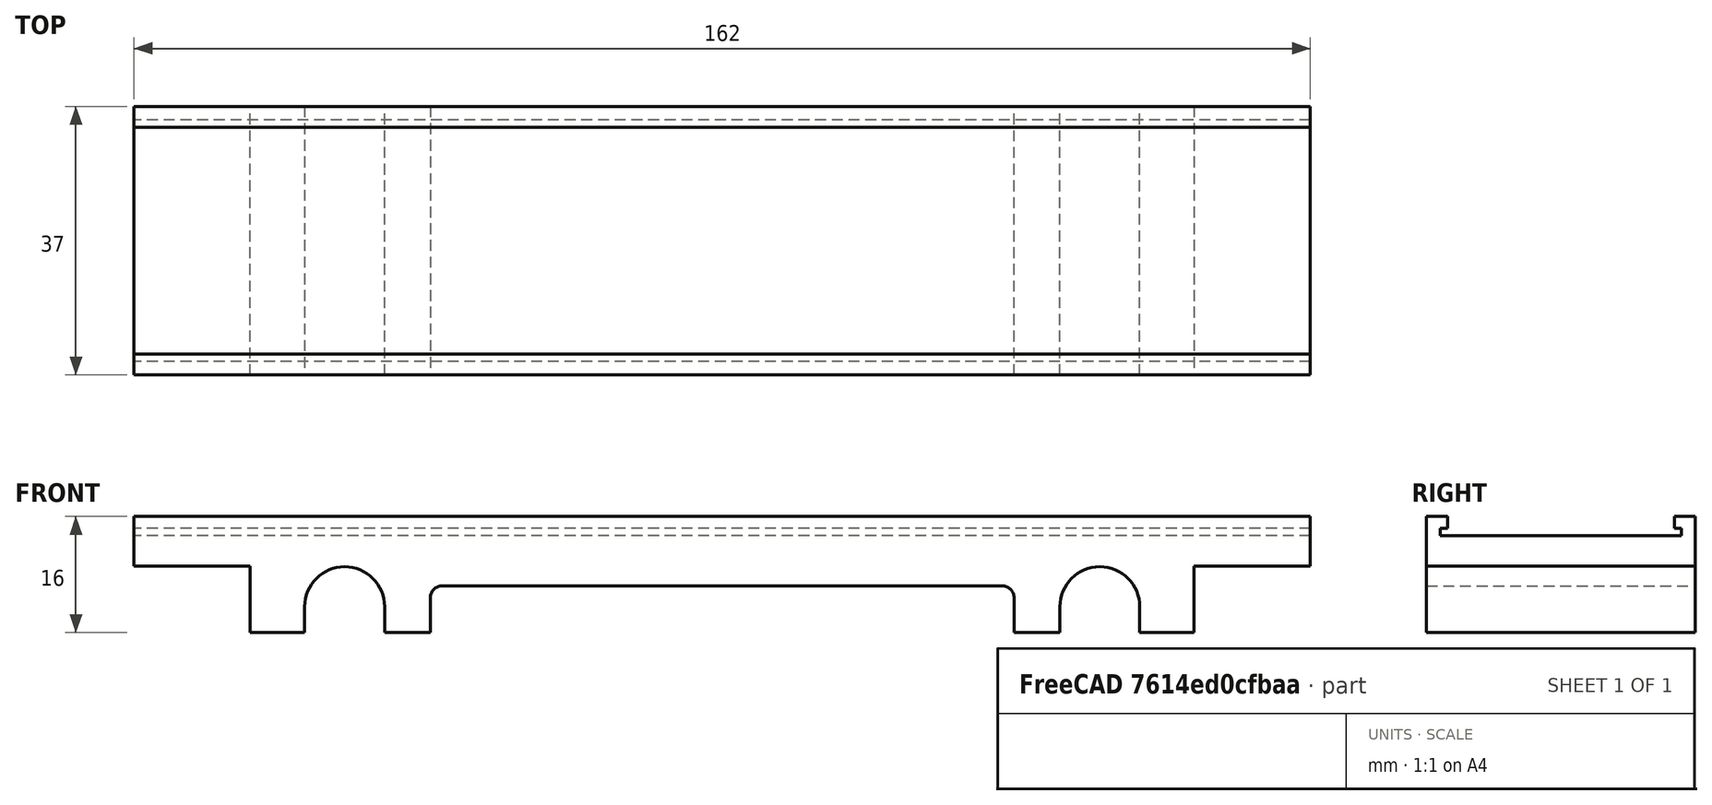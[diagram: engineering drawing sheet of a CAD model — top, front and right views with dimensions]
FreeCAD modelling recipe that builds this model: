
FCSTD DOCUMENT  (FreeCAD 0.20R29603 (Git))
Label: Enroute Strip Holder
License: All rights reserved
LicenseURL: http://en.wikipedia.org/wiki/All_rights_reserved
objects: TechDraw::DrawViewDimension×19, Sketcher::SketchObject×8, PartDesign::Pocket×7, TechDraw::DrawViewPart×5, PartDesign::Pad×1, PartDesign::Body×1, App::Part×1, TechDraw::DrawSVGTemplate×1, TechDraw::DrawPage×1
note: 25 computed .brp shape members not serialized (recipe doc carries the construction recipe); baked Part::Feature solids carry a one-line shape summary decoded from their .brp

FEATURE [Sketcher::SketchObject] Sketch
  FullyConstrained = true
  MapMode = 5
  Support = -> [XY_Plane001]
  sketch-geometry (5):
    g0: LineSegment StartX=-81 StartY=18.5 StartZ=0 EndX=-81 EndY=-18.5 EndZ=0
    g1: LineSegment StartX=-81 StartY=-18.5 StartZ=0 EndX=81 EndY=-18.5 EndZ=0
    g2: LineSegment StartX=81 StartY=-18.5 StartZ=0 EndX=81 EndY=18.5 EndZ=0
    g3: LineSegment StartX=81 StartY=18.5 StartZ=0 EndX=-81 EndY=18.5 EndZ=0
    g4: GeomPoint X=0 Y=0 Z=0
  constraints (12):
    c: Coincident(g0,g1)
    c: Coincident(g1,g2)
    c: Coincident(g2,g3)
    c: Coincident(g3,g0)
    c: Horizontal(g1)
    c: Horizontal(g3)
    c: Vertical(g0)
    c: Vertical(g2)
    c: Symmetric(g1,g0,g4)
    c: Coincident(g4,g-1)
    c: DistanceY(g2,g2) = 37
    c: DistanceX(g3,g3) = 162
FEATURE [PartDesign::Pad] Pad
  Direction = (0,0,1)
  Length = 16
  Length2 = 10
  Profile = -> Sketch
  ReferenceAxis = -> Sketch [N_Axis]
  Type = 0
FEATURE [Sketcher::SketchObject] Sketch001
  ExternalGeometry = -> [Pad]
  FullyConstrained = true
  MapMode = 5
  Placement = pos=(0,0,0) rot=(1,0,0;1.5708rad)
  Support = -> [XZ_Plane001]
  sketch-geometry (6):
    g0: LineSegment StartX=81 StartY=16 StartZ=0 EndX=81 EndY=9.14 EndZ=0
    g1: LineSegment StartX=81 StartY=9.14 StartZ=0 EndX=65 EndY=9.14 EndZ=0
    g2: LineSegment StartX=65 StartY=9.14 StartZ=0 EndX=65 EndY=-1.45 EndZ=0
    g3: LineSegment StartX=81 StartY=16 StartZ=0 EndX=83.75 EndY=16 EndZ=0
    g4: LineSegment StartX=83.75 StartY=16 StartZ=0 EndX=83.75 EndY=-1.45 EndZ=0
    g5: LineSegment StartX=65 StartY=-1.45 StartZ=0 EndX=83.75 EndY=-1.45 EndZ=0
  constraints (17):
    c: Coincident(g0,g1)
    c: Coincident(g1,g2)
    c: Vertical(g0)
    c: DistanceY(g0,g0) = 6.86
    c: Horizontal(g1)
    c: Vertical(g2)
    c: DistanceX(g1,g1) = 16
    c: Coincident(g0,g-3)
    c: Coincident(g0,g3)
    c: Horizontal(g3)
    c: Coincident(g3,g4)
    c: Vertical(g4)
    c: Horizontal(g4,g2)
    c: Coincident(g2,g5)
    c: Coincident(g5,g4)
    c: DistanceY(g4,g4) = 17.45
    c: DistanceX(g5,g5) = 18.75
FEATURE [Sketcher::SketchObject] MirroredSketch
  FullyConstrained = false
  Placement = pos=(0,0,0) rot=(1,0,0;1.5708rad)
  sketch-geometry (6):
    g0: LineSegment StartX=-81 StartY=16 StartZ=0 EndX=-81 EndY=9.14 EndZ=0
    g1: LineSegment StartX=-81 StartY=9.14 StartZ=0 EndX=-65 EndY=9.14 EndZ=0
    g2: LineSegment StartX=-65 StartY=9.14 StartZ=0 EndX=-65 EndY=-1.45 EndZ=0
    g3: LineSegment StartX=-81 StartY=16 StartZ=0 EndX=-83.75 EndY=16 EndZ=0
    g4: LineSegment StartX=-83.75 StartY=16 StartZ=0 EndX=-83.75 EndY=-1.45 EndZ=0
    g5: LineSegment StartX=-65 StartY=-1.45 StartZ=0 EndX=-83.75 EndY=-1.45 EndZ=0
  constraints (11):
    c: Coincident(g0,g1)
    c: Coincident(g1,g2)
    c: Vertical(g0)
    c: Horizontal(g1)
    c: Vertical(g2)
    c: Coincident(g0,g3)
    c: Horizontal(g3)
    c: Coincident(g3,g4)
    c: Vertical(g4)
    c: Coincident(g2,g5)
    c: Coincident(g5,g4)
FEATURE [PartDesign::Pocket] Pocket
  BaseFeature = -> Pad
  Direction = (0,1,-2e-16)
  Length = 5
  Length2 = 5
  Midplane = true
  Profile = -> Sketch001
  ReferenceAxis = -> Sketch001 [N_Axis]
  Type = 1
FEATURE [PartDesign::Pocket] Pocket001
  BaseFeature = -> Pocket
  Direction = (0,1,0)
  Length = 5
  Length2 = 5
  Midplane = true
  Profile = -> MirroredSketch
  ReferenceAxis = -> MirroredSketch [N_Axis]
  Type = 1
FEATURE [Sketcher::SketchObject] Sketch002
  ExternalGeometry = -> [Pocket001]
  FullyConstrained = true
  MapMode = 5
  Placement = pos=(0,0,0) rot=(1,0,0;1.5708rad)
  Support = -> [XZ_Plane001]
  sketch-geometry (4):
    g0: LineSegment StartX=57.5 StartY=3.58 StartZ=0 EndX=57.5 EndY=-2.6 EndZ=0
    g1: LineSegment StartX=57.5 StartY=-2.6 StartZ=0 EndX=46.5 EndY=-2.6 EndZ=0
    g2: LineSegment StartX=46.5 StartY=-2.6 StartZ=0 EndX=46.5 EndY=3.58 EndZ=0
    g3: ArcOfCircle CenterX=52 CenterY=3.58 CenterZ=0 NormalX=0 NormalY=0 NormalZ=1 AngleXU=0 Radius=5.5 StartAngle=0 EndAngle=3.14159
  constraints (12):
    c: Coincident(g0,g1)
    c: Coincident(g1,g2)
    c: Vertical(g2)
    c: Vertical(g0)
    c: Horizontal(g1)
    c: DistanceY(g0,g0) = 6.18
    c: Tangent(g2,g3) = 1.5708
    c: Coincident(g3,g0)
    c: Horizontal(g3,g0)
    c: DistanceX(g3,g-3) = 29
    c: DistanceX(g1,g1) = 11
    c: DistanceY(g-4,g3) = 3.58
FEATURE [PartDesign::Pocket] Pocket002
  BaseFeature = -> Pocket001
  Direction = (0,1,-2e-16)
  Length = 5
  Length2 = 5
  Midplane = true
  Profile = -> Sketch002
  ReferenceAxis = -> Sketch002 [N_Axis]
  Type = 1
FEATURE [Sketcher::SketchObject] MirroredSketch001
  FullyConstrained = false
  Placement = pos=(0,0,0) rot=(1,0,0;1.5708rad)
  sketch-geometry (4):
    g0: LineSegment StartX=-57.5 StartY=3.58 StartZ=0 EndX=-57.5 EndY=-2.6 EndZ=0
    g1: LineSegment StartX=-57.5 StartY=-2.6 StartZ=0 EndX=-46.5 EndY=-2.6 EndZ=0
    g2: LineSegment StartX=-46.5 StartY=-2.6 StartZ=0 EndX=-46.5 EndY=3.58 EndZ=0
    g3: ArcOfCircle CenterX=-52 CenterY=3.58 CenterZ=0 NormalX=0 NormalY=0 NormalZ=1 AngleXU=0 Radius=5.5 StartAngle=2e-16 EndAngle=3.14159
  constraints (7):
    c: Coincident(g0,g1)
    c: Coincident(g1,g2)
    c: Vertical(g2)
    c: Vertical(g0)
    c: Horizontal(g1)
    c: Tangent(g2,g3) = -1.5708
    c: Coincident(g3,g0)
FEATURE [PartDesign::Pocket] Pocket003
  BaseFeature = -> Pocket002
  Direction = (0,1,0)
  Length = 5
  Length2 = 5
  Midplane = true
  Profile = -> MirroredSketch001
  ReferenceAxis = -> MirroredSketch001 [N_Axis]
  Type = 1
FEATURE [Sketcher::SketchObject] Sketch003
  ExternalGeometry = -> [Pocket003]
  FullyConstrained = true
  MapMode = 5
  Placement = pos=(0,0,0) rot=(1,0,0;1.5708rad)
  Support = -> [XZ_Plane001]
  sketch-geometry (7):
    g0: LineSegment StartX=-40.2 StartY=4.78 StartZ=0 EndX=-40.2 EndY=-1.94 EndZ=0
    g1: LineSegment StartX=-40.2 StartY=-1.94 StartZ=0 EndX=40.2 EndY=-1.94 EndZ=0
    g2: LineSegment StartX=40.2 StartY=-1.94 StartZ=0 EndX=40.2 EndY=4.78 EndZ=0
    g3: LineSegment StartX=38.52 StartY=6.46 StartZ=0 EndX=-38.52 EndY=6.46 EndZ=0
    g4: GeomPoint X=0 Y=0 Z=0
    g5: ArcOfCircle CenterX=-38.52 CenterY=4.78 CenterZ=0 NormalX=0 NormalY=0 NormalZ=1 AngleXU=0 Radius=1.68 StartAngle=1.5708 EndAngle=3.14159
    g6: ArcOfCircle CenterX=38.52 CenterY=4.78 CenterZ=0 NormalX=0 NormalY=0 NormalZ=1 AngleXU=0 Radius=1.68 StartAngle=0 EndAngle=1.5708
  constraints (17):
    c: Coincident(g0,g1)
    c: Coincident(g1,g2)
    c: Horizontal(g1)
    c: Horizontal(g3)
    c: Vertical(g0)
    c: Vertical(g2)
    c: Coincident(g4,g-1)
    c: DistanceX(g-3,g0) = 6.3
    c: Tangent(g0,g5) = -1.5708
    c: Tangent(g3,g5) = -1.5708
    c: Tangent(g2,g6) = -1.5708
    c: Tangent(g3,g6) = -1.5708
    c: Equal(g6,g5)
    c: DistanceY(g3,g-5) = 9.54
    c: DistanceX(g1,g-4) = 6.3
    c: DistanceY(g0,g3) = 1.68
    c: DistanceY(g0,g0) = 6.72
FEATURE [PartDesign::Pocket] Pocket004
  BaseFeature = -> Pocket003
  Direction = (0,1,-2e-16)
  Length = 5
  Length2 = 5
  Midplane = true
  Profile = -> Sketch003
  ReferenceAxis = -> Sketch003 [N_Axis]
  Type = 1
FEATURE [Sketcher::SketchObject] Sketch004
  ExternalGeometry = -> [Pocket004]
  FullyConstrained = true
  MapMode = 5
  Placement = pos=(0,0,0) rot=(0.57735,0.57735,0.57735;2.0944rad)
  Support = -> [YZ_Plane001]
  sketch-geometry (4):
    g0: LineSegment StartX=-15.62 StartY=17.28 StartZ=0 EndX=15.62 EndY=17.28 EndZ=0
    g1: LineSegment StartX=15.62 StartY=17.28 StartZ=0 EndX=15.62 EndY=13.36 EndZ=0
    g2: LineSegment StartX=15.62 StartY=13.36 StartZ=0 EndX=-15.62 EndY=13.36 EndZ=0
    g3: LineSegment StartX=-15.62 StartY=13.36 StartZ=0 EndX=-15.62 EndY=17.28 EndZ=0
  constraints (12):
    c: Coincident(g0,g1)
    c: Coincident(g1,g2)
    c: Coincident(g2,g3)
    c: Coincident(g3,g0)
    c: Horizontal(g0)
    c: Horizontal(g2)
    c: Vertical(g1)
    c: Vertical(g3)
    c: DistanceY(g1,g-4) = 2.64
    c: DistanceX(g1,g-4) = 2.88
    c: DistanceX(g-3,g2) = 2.88
    c: DistanceY(g3,g3) = 3.92
FEATURE [PartDesign::Pocket] Pocket005
  BaseFeature = -> Pocket004
  Direction = (-1,2e-16,-3e-16)
  Length = 5
  Length2 = 5
  Midplane = true
  Profile = -> Sketch004
  ReferenceAxis = -> Sketch004 [N_Axis]
  Type = 1
FEATURE [Sketcher::SketchObject] Sketch005
  ExternalGeometry = -> [Pocket005]
  FullyConstrained = true
  MapMode = 5
  Placement = pos=(0,0,0) rot=(0.57735,0.57735,0.57735;2.0944rad)
  Support = -> [YZ_Plane001]
  sketch-geometry (4):
    g0: LineSegment StartX=-16.62 StartY=14.36 StartZ=0 EndX=16.62 EndY=14.36 EndZ=0
    g1: LineSegment StartX=16.62 StartY=14.36 StartZ=0 EndX=16.62 EndY=13.36 EndZ=0
    g2: LineSegment StartX=16.62 StartY=13.36 StartZ=0 EndX=-16.62 EndY=13.36 EndZ=0
    g3: LineSegment StartX=-16.62 StartY=13.36 StartZ=0 EndX=-16.62 EndY=14.36 EndZ=0
  constraints (12):
    c: Coincident(g0,g1)
    c: Coincident(g1,g2)
    c: Coincident(g2,g3)
    c: Coincident(g3,g0)
    c: Horizontal(g0)
    c: Horizontal(g2)
    c: Vertical(g1)
    c: Vertical(g3)
    c: Horizontal(g2,g-3)
    c: DistanceX(g2,g-3) = 1
    c: DistanceX(g-4,g1) = 1
    c: DistanceY(g3,g3) = 1
FEATURE [PartDesign::Pocket] Pocket006
  BaseFeature = -> Pocket005
  Direction = (-1,2e-16,-3e-16)
  Length = 5
  Length2 = 5
  Midplane = true
  Profile = -> Sketch005
  ReferenceAxis = -> Sketch005 [N_Axis]
  Type = 1
FEATURE [PartDesign::Body] Body
  Group = -> [Sketch,Pad,Sketch001,Pocket,MirroredSketch,Pocket001,Sketch002,Pocket002,MirroredSketch001,Pocket003,Sketch003,Pocket004,Sketch004,Pocket005,Sketch005,Pocket006]
  Origin = -> Origin001
  Tip = -> Pocket006
FEATURE [App::Part] Part
  Group = -> [Body]
  Origin = -> Origin
FEATURE [TechDraw::DrawSVGTemplate] Template
  EditableTexts = Designed_by_Name=MR; FC-Date=23 AUG 23; FC-SC=0.75; FC-SH=1 of 1; FC-Title=3D Enroute Strip Holder; Subtitle=3D Enroute Strip Technical Drawing
  Height = 215.9
  Orientation = 1
  Width = 279.4
FEATURE [TechDraw::DrawViewPart] View  label="View 1"
  Caption = View 1
  CoarseView = false
  Direction = (0.438,-0.682,0.587)
  Focus = 100
  HardHidden = false
  IsoCount = 0
  IsoHidden = false
  IsoVisible = false
  LockPosition = false
  Perspective = true
  Rotation = 0
  Scale = 0.5
  ScaleType = 2
  SeamHidden = false
  SeamVisible = true
  SmoothHidden = false
  SmoothVisible = true
  Source = -> [Pocket006]
  X = 211.958
  XDirection = (0.812,0.58,0.068)
  Y = 163.392
FEATURE [TechDraw::DrawViewPart] View001  label="Side View"
  Caption = Side View
  CoarseView = false
  Direction = (0,-1,0)
  Focus = 100
  HardHidden = false
  IsoCount = 0
  IsoHidden = false
  IsoVisible = false
  LockPosition = false
  Perspective = false
  Rotation = 0
  Scale = 0.75
  ScaleType = 2
  SeamHidden = false
  SeamVisible = true
  SmoothHidden = false
  SmoothVisible = true
  Source = -> [Pocket006]
  X = 127.726
  XDirection = (1,0,0)
  Y = 118.064
FEATURE [TechDraw::DrawViewPart] View002  label="Top View"
  Caption = Top VIew
  CoarseView = false
  Direction = (0,0,1)
  Focus = 100
  HardHidden = false
  IsoCount = 0
  IsoHidden = false
  IsoVisible = false
  LockPosition = false
  Perspective = false
  Rotation = 0
  Scale = 0.75
  ScaleType = 2
  SeamHidden = false
  SeamVisible = true
  SmoothHidden = false
  SmoothVisible = true
  Source = -> [Pocket006]
  X = 95.4276
  XDirection = (1,0,0)
  Y = 171.953
FEATURE [TechDraw::DrawViewDimension] Dimension
  AngleOverride = false
  Arbitrary = false
  ArbitraryTolerances = false
  EqualTolerance = true
  ExtensionAngle = 0
  FormatSpec = %.2w
  FormatSpecOverTolerance = %+.2w
  FormatSpecUnderTolerance = %+.2w
  Inverted = false
  LineAngle = 0
  LockPosition = false
  MeasureType = 1
  OverTolerance = 0
  References2D = -> [View002]
  Rotation = 0
  ScaleType = 0
  TheoreticalExact = false
  Type = 2
  UnderTolerance = 0
  X = -69.373
  Y = -33.7587
FEATURE [TechDraw::DrawViewDimension] Dimension001
  AngleOverride = false
  Arbitrary = false
  ArbitraryTolerances = false
  EqualTolerance = true
  ExtensionAngle = 0
  FormatSpec = %.2w
  FormatSpecOverTolerance = %+.2w
  FormatSpecUnderTolerance = %+.2w
  Inverted = false
  LineAngle = 0
  LockPosition = false
  MeasureType = 1
  OverTolerance = 0
  References2D = -> [View002]
  Rotation = 0
  ScaleType = 0
  TheoreticalExact = false
  Type = 2
  UnderTolerance = 0
  X = -61.7297
  Y = -31.8763
FEATURE [TechDraw::DrawViewDimension] Dimension002
  AngleOverride = false
  Arbitrary = false
  ArbitraryTolerances = false
  EqualTolerance = true
  ExtensionAngle = 0
  FormatSpec = %.2w
  FormatSpecOverTolerance = %+.2w
  FormatSpecUnderTolerance = %+.2w
  Inverted = false
  LineAngle = 0
  LockPosition = false
  MeasureType = 1
  OverTolerance = 0
  References2D = -> [View002]
  Rotation = 0
  ScaleType = 0
  TheoreticalExact = false
  Type = 2
  UnderTolerance = 0
  X = -53.9294
  Y = -34.0912
FEATURE [TechDraw::DrawViewDimension] Dimension003
  AngleOverride = false
  Arbitrary = false
  ArbitraryTolerances = false
  EqualTolerance = true
  ExtensionAngle = 0
  FormatSpec = %.2w
  FormatSpecOverTolerance = %+.2w
  FormatSpecUnderTolerance = %+.2w
  Inverted = false
  LineAngle = 0
  LockPosition = false
  MeasureType = 1
  OverTolerance = 0
  References2D = -> [View002]
  Rotation = 0
  ScaleType = 0
  TheoreticalExact = false
  Type = 1
  UnderTolerance = 0
  X = -1.23363
  Y = 4.65436
FEATURE [TechDraw::DrawViewDimension] Dimension004
  AngleOverride = false
  Arbitrary = false
  ArbitraryTolerances = false
  EqualTolerance = true
  ExtensionAngle = 0
  FormatSpec = %.2w
  FormatSpecOverTolerance = %+.2w
  FormatSpecUnderTolerance = %+.2w
  Inverted = false
  LineAngle = 0
  LockPosition = false
  MeasureType = 1
  OverTolerance = 0
  References2D = -> [View001]
  Rotation = 0
  ScaleType = 0
  TheoreticalExact = false
  Type = 2
  UnderTolerance = 0
  X = -73.1651
  Y = -23.1108
FEATURE [TechDraw::DrawViewDimension] Dimension005
  AngleOverride = false
  Arbitrary = false
  ArbitraryTolerances = false
  EqualTolerance = true
  ExtensionAngle = 0
  FormatSpec = %.2w
  FormatSpecOverTolerance = %+.2w
  FormatSpecUnderTolerance = %+.2w
  Inverted = false
  LineAngle = 0
  LockPosition = false
  MeasureType = 1
  OverTolerance = 0
  References2D = -> [View001]
  Rotation = 0
  ScaleType = 0
  TheoreticalExact = false
  Type = 2
  UnderTolerance = 0
  X = -67.4232
  Y = -22.9238
FEATURE [TechDraw::DrawViewDimension] Dimension006
  AngleOverride = false
  Arbitrary = false
  ArbitraryTolerances = false
  EqualTolerance = true
  ExtensionAngle = 0
  FormatSpec = %.2w
  FormatSpecOverTolerance = %+.2w
  FormatSpecUnderTolerance = %+.2w
  Inverted = false
  LineAngle = 0
  LockPosition = false
  MeasureType = 1
  OverTolerance = 0
  References2D = -> [View001]
  Rotation = 0
  ScaleType = 0
  TheoreticalExact = false
  Type = 1
  UnderTolerance = 0
  X = -31.5451
  Y = -29.8003
FEATURE [TechDraw::DrawViewDimension] Dimension007
  AngleOverride = false
  Arbitrary = false
  ArbitraryTolerances = false
  EqualTolerance = true
  ExtensionAngle = 0
  FormatSpec = %.2w
  FormatSpecOverTolerance = %+.2w
  FormatSpecUnderTolerance = %+.2w
  Inverted = false
  LineAngle = 0
  LockPosition = false
  MeasureType = 1
  OverTolerance = 0
  References2D = -> [View001]
  Rotation = 0
  ScaleType = 0
  TheoreticalExact = false
  Type = 1
  UnderTolerance = 0
  X = -21.2508
  Y = -20.8359
FEATURE [TechDraw::DrawViewDimension] Dimension008
  AngleOverride = false
  Arbitrary = false
  ArbitraryTolerances = false
  EqualTolerance = true
  ExtensionAngle = 0
  FormatSpec = %.2w
  FormatSpecOverTolerance = %+.2w
  FormatSpecUnderTolerance = %+.2w
  Inverted = false
  LineAngle = 0
  LockPosition = false
  MeasureType = 1
  OverTolerance = 0
  References2D = -> [View001]
  Rotation = 0
  ScaleType = 0
  TheoreticalExact = false
  Type = 1
  UnderTolerance = 0
  X = -20.8366
  Y = -13.2299
FEATURE [TechDraw::DrawViewDimension] Dimension009
  AngleOverride = false
  Arbitrary = false
  ArbitraryTolerances = false
  EqualTolerance = true
  ExtensionAngle = 0
  FormatSpec = %.2w
  FormatSpecOverTolerance = %+.2w
  FormatSpecUnderTolerance = %+.2w
  Inverted = false
  LineAngle = 0
  LockPosition = false
  MeasureType = 1
  OverTolerance = 0
  References2D = -> [View001]
  Rotation = 0
  ScaleType = 0
  TheoreticalExact = false
  Type = 1
  UnderTolerance = 0
  X = -34.6415
  Y = 22.004
FEATURE [TechDraw::DrawViewDimension] Dimension010
  AngleOverride = false
  Arbitrary = false
  ArbitraryTolerances = false
  EqualTolerance = true
  ExtensionAngle = 0
  FormatSpec = %.2w
  FormatSpecOverTolerance = %+.2w
  FormatSpecUnderTolerance = %+.2w
  Inverted = false
  LineAngle = 0
  LockPosition = false
  MeasureType = 1
  OverTolerance = 0
  References2D = -> [View001]
  Rotation = 0
  ScaleType = 0
  TheoreticalExact = false
  Type = 1
  UnderTolerance = 0
  X = -16.469
  Y = 17.1622
FEATURE [TechDraw::DrawViewDimension] Dimension011
  AngleOverride = false
  Arbitrary = false
  ArbitraryTolerances = false
  EqualTolerance = true
  ExtensionAngle = 0
  FormatSpec = %.2w
  FormatSpecOverTolerance = %+.2w
  FormatSpecUnderTolerance = %+.2w
  Inverted = false
  LineAngle = 0
  LockPosition = false
  MeasureType = 1
  OverTolerance = 0
  References2D = -> [View001]
  Rotation = 0
  ScaleType = 0
  TheoreticalExact = false
  Type = 1
  UnderTolerance = 0
  X = 0.135137
  Y = -2.14863
FEATURE [TechDraw::DrawViewDimension] Dimension012
  AngleOverride = false
  Arbitrary = false
  ArbitraryTolerances = false
  EqualTolerance = true
  ExtensionAngle = 0
  FormatSpec = %.2w
  FormatSpecOverTolerance = %+.2w
  FormatSpecUnderTolerance = %+.2w
  Inverted = false
  LineAngle = 0
  LockPosition = false
  MeasureType = 1
  OverTolerance = 0
  References2D = -> [View001]
  Rotation = 0
  ScaleType = 0
  TheoreticalExact = false
  Type = 1
  UnderTolerance = 0
  X = 0.616815
  Y = 5.66271
FEATURE [TechDraw::DrawViewPart] View003  label="View 2"
  Caption = View 2
  CoarseView = false
  Direction = (-0.577,0.577,-0.577)
  Focus = 100
  HardHidden = false
  IsoCount = 0
  IsoHidden = false
  IsoVisible = false
  LockPosition = false
  Perspective = true
  Rotation = 0
  Scale = 0.5
  ScaleType = 2
  SeamHidden = false
  SeamVisible = true
  SmoothHidden = false
  SmoothVisible = true
  Source = -> [Pocket006]
  X = 217.742
  XDirection = (0.789,0.211,-0.577)
  Y = 71.6514
FEATURE [TechDraw::DrawViewPart] View004  label="End View"
  Caption = End View
  CoarseView = false
  Direction = (1,0,0)
  Focus = 100
  HardHidden = false
  IsoCount = 0
  IsoHidden = false
  IsoVisible = false
  LockPosition = false
  Perspective = false
  Rotation = 0
  Scale = 0.75
  ScaleType = 2
  SeamHidden = false
  SeamVisible = true
  SmoothHidden = false
  SmoothVisible = true
  Source = -> [Pocket006]
  X = 68.1609
  XDirection = (0,1,0)
  Y = 44.6778
FEATURE [TechDraw::DrawViewDimension] Dimension013
  AngleOverride = false
  Arbitrary = false
  ArbitraryTolerances = false
  EqualTolerance = true
  ExtensionAngle = 0
  FormatSpec = %.2w
  FormatSpecOverTolerance = %+.2w
  FormatSpecUnderTolerance = %+.2w
  Inverted = false
  LineAngle = 0
  LockPosition = false
  MeasureType = 1
  OverTolerance = 0
  References2D = -> [View004]
  Rotation = 0
  ScaleType = 0
  TheoreticalExact = false
  Type = 2
  UnderTolerance = 0
  X = -36.7345
  Y = -7.95862
FEATURE [TechDraw::DrawViewDimension] Dimension016
  AngleOverride = false
  Arbitrary = false
  ArbitraryTolerances = false
  EqualTolerance = true
  ExtensionAngle = 0
  FormatSpec = %.2w
  FormatSpecOverTolerance = %+.2w
  FormatSpecUnderTolerance = %+.2w
  Inverted = false
  LineAngle = 0
  LockPosition = false
  MeasureType = 1
  OverTolerance = 0
  References2D = -> [View004]
  Rotation = 0
  ScaleType = 0
  TheoreticalExact = false
  Type = 1
  UnderTolerance = 0
  X = 32.2773
  Y = -16.613
FEATURE [TechDraw::DrawViewDimension] Dimension017
  AngleOverride = false
  Arbitrary = false
  ArbitraryTolerances = false
  EqualTolerance = true
  ExtensionAngle = 0
  FormatSpec = %.2w
  FormatSpecOverTolerance = %+.2w
  FormatSpecUnderTolerance = %+.2w
  Inverted = false
  LineAngle = 0
  LockPosition = false
  MeasureType = 1
  OverTolerance = 0
  References2D = -> [View004]
  Rotation = 0
  ScaleType = 0
  TheoreticalExact = false
  Type = 1
  UnderTolerance = 0
  X = -27.5854
  Y = 24.3041
FEATURE [TechDraw::DrawViewDimension] Dimension018
  AngleOverride = false
  Arbitrary = false
  ArbitraryTolerances = false
  EqualTolerance = true
  ExtensionAngle = 0
  FormatSpec = %.2w
  FormatSpecOverTolerance = %+.2w
  FormatSpecUnderTolerance = %+.2w
  Inverted = false
  LineAngle = 0
  LockPosition = false
  MeasureType = 1
  OverTolerance = 0
  References2D = -> [View004]
  Rotation = 0
  ScaleType = 0
  TheoreticalExact = false
  Type = 1
  UnderTolerance = 0
  X = 35.152
  Y = 17.3547
FEATURE [TechDraw::DrawViewDimension] Dimension019
  AngleOverride = false
  Arbitrary = false
  ArbitraryTolerances = false
  EqualTolerance = true
  ExtensionAngle = 0
  FormatSpec = %.2w
  FormatSpecOverTolerance = %+.2w
  FormatSpecUnderTolerance = %+.2w
  Inverted = false
  LineAngle = 0
  LockPosition = false
  MeasureType = 1
  OverTolerance = 0
  References2D = -> [View001]
  Rotation = 0
  ScaleType = 0
  TheoreticalExact = false
  Type = 2
  UnderTolerance = 0
  X = 63.5613
  Y = 21.2365
FEATURE [TechDraw::DrawViewDimension] Dimension020
  AngleOverride = false
  Arbitrary = false
  ArbitraryTolerances = false
  EqualTolerance = true
  ExtensionAngle = 0
  FormatSpec = %.2w
  FormatSpecOverTolerance = %+.2w
  FormatSpecUnderTolerance = %+.2w
  Inverted = false
  LineAngle = 0
  LockPosition = false
  MeasureType = 1
  OverTolerance = 0
  References2D = -> [View004]
  Rotation = 0
  ScaleType = 0
  TheoreticalExact = false
  Type = 2
  UnderTolerance = 0
  X = -29.406
  Y = -10.5833
FEATURE [TechDraw::DrawPage] Page
  KeepUpdated = true
  NextBalloonIndex = 1
  ProjectionType = 0
  Template = -> Template
  Views = -> [View,View001,View002,Dimension,Dimension001,Dimension002,Dimension003,Dimension004,Dimension005,Dimension006,Dimension007,Dimension008,Dimension009,Dimension010,Dimension011,Dimension012,View003,View004,Dimension013,Dimension016,Dimension017,Dimension018,Dimension019,Dimension020]
